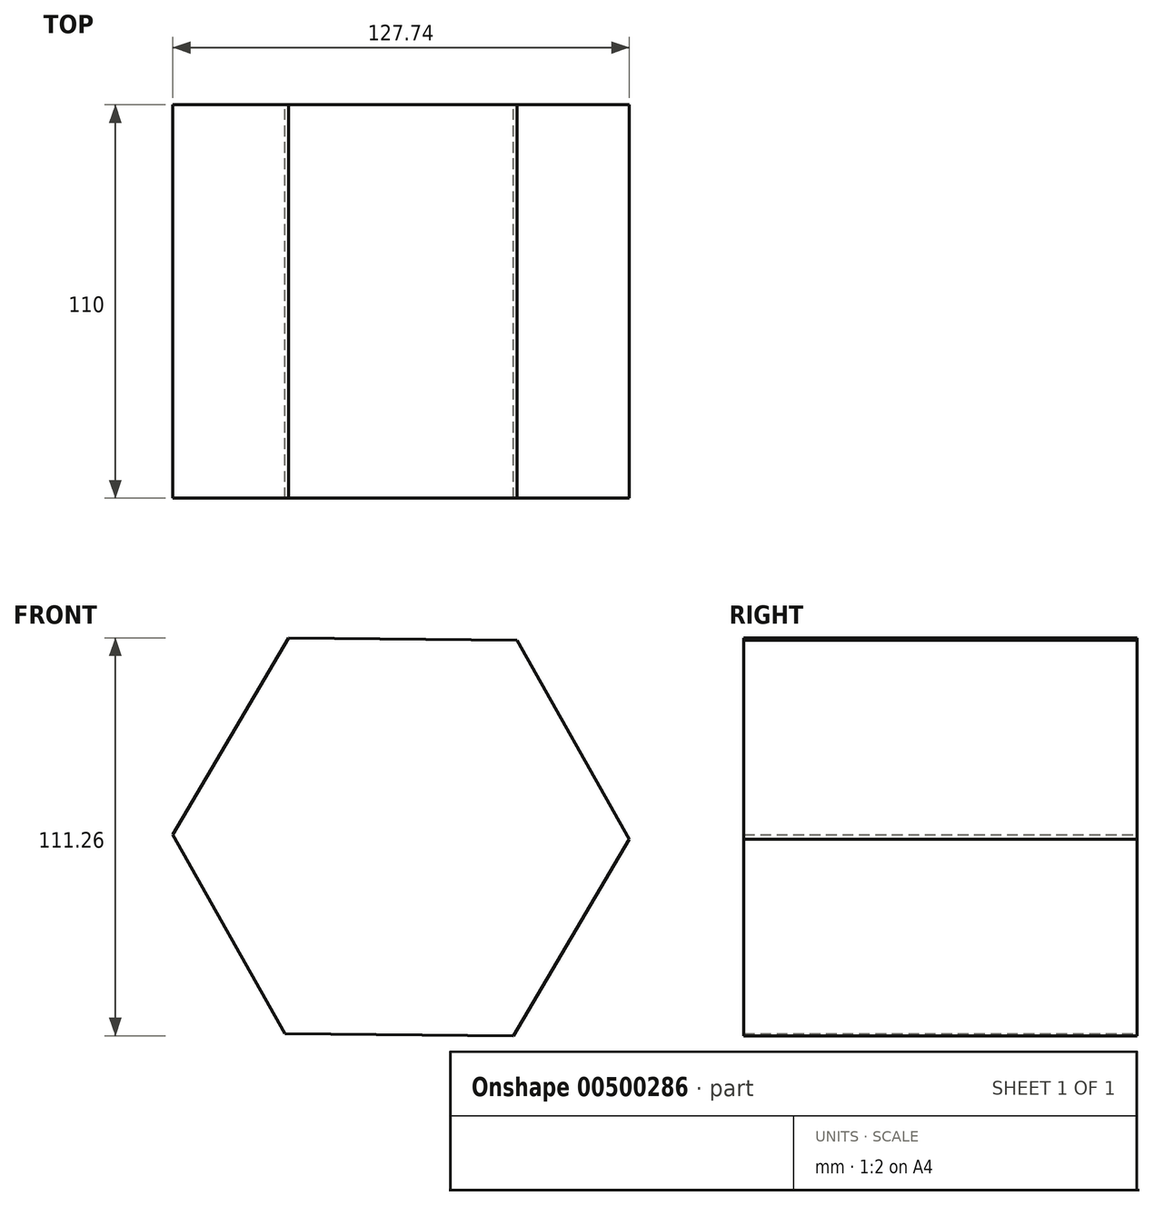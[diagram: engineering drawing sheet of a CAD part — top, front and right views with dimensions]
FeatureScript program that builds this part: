
annotation { "Feature Type Name" : "Feature", "Feature Type Description" : "" }
export const myFeature = defineFeature(function(context is Context, id is Id, definition is map)
    precondition{}
    {
        {
            var Q0;
            Q0=qCreatedBy(makeId("Front.planeOp"),FACE);
            var sketch = newSketch(context, id + "F0", { "sketchPlane" : qUnion([Q0])});
            skCircle(sketch, "E0.cCircle", {"center": v(0, 0) * mm, "radius": 63.87 * mm, "construction": true});
            skLineSegment(sketch, "E0.0", {"start": v(-31.4, 55.63) * mm, "end": v(32.48, 55) * mm});
            skLineSegment(sketch, "E0.1", {"start": v(32.48, 55) * mm, "end": v(63.87, -0.62) * mm});
            skLineSegment(sketch, "E0.2", {"start": v(63.87, -0.62) * mm, "end": v(31.4, -55.63) * mm});
            skLineSegment(sketch, "E0.3", {"start": v(31.4, -55.63) * mm, "end": v(-32.48, -55) * mm});
            skLineSegment(sketch, "E0.4", {"start": v(-32.48, -55) * mm, "end": v(-63.87, 0.62) * mm});
            skLineSegment(sketch, "E0.5", {"start": v(-63.87, 0.62) * mm, "end": v(-31.4, 55.63) * mm});
            skSolve(sketch);
        }
        {
            var Q0;
            Q0=makeQuery(id+"F0.imprint","IMPRINT",FACE,{"disambiguationData":[TD([[makeQuery(id+"F0.imprint","IMPRINT",EDGE,{"derivedFrom":sQuery(id+"F0.wireOp",EDGE,"E0.0")}),-1.0]])]});
            extrude(context, id + "F1", {"entities" : qUnion([Q0]), "depth" : 110 * mm});
        }
    });
